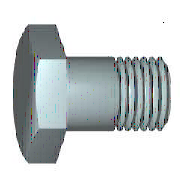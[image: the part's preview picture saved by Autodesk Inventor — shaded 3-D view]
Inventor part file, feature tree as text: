
AUTODESK INVENTOR PART (.ipt)
format: ipt  version: 2021 (Build 250183000, 183)  size: 188,928 bytes
history: native  units: mm (DEFAULTED — no unit token found)
features: sketch x3, extrude x1, chamfer x1, plane x1
ambient origin geometry x7: Origin, YZ Plane, XZ Plane, X Axis, Y Axis, Z Axis, Center Point
bodies: Solid1 (feature_tree), Body (feature_tree)
feature tree (6):
  extrude  "Head"  Depth=18.0mm
  chamfer  "Chamfer1"  Distance=3.5mm
  plane  "Work Plane1"
  sketch  "Sketch1"  dims[d0=60.0mm d1=18.0mm]
  sketch  "Sketch2"  dims[d2=6.0mm]
  sketch  "Sketch4"  dims[d12=90.0deg d3=3.5mm d4=0.0mm d5=30.0deg d21=90.0deg d6=0.61345mm d7=0.61355mm d8=0.0mm d9=0.5001mm d10=8.88mm d11=10.0mm d13=0.61355mm d14=6.0mm d15=18.0mm d16=0.0mm d19=10.0mm d55=45.0deg d57=0.0mm d58=0.0mm]
